# Revit family: Gleitschlitte Typ A, höhe h=100mm, Ø219 bis Ø457mm, o.D.
name_source: partatom
category: HLS-Bauteile
revit_build: Autodesk Revit 2018 (Build: 20190510_1515(x64)
units: mm (PartAtom-declared; Revit-internal decimal feet)

## family parameters
Arbeitsebenenbasiert = Ja
Beim Laden mit Abzugskörper schneiden = Nein
Bemaßung runder Anschluss = Durchmesser verwenden
Gemeinsam genutzt = Ja
Immer vertikal = Nein
Klassifizierung = Keine
Raumberechnungspunkt = Nein
Teiletyp = Normal

## types (11) — shared parameters
Breite Schellenband = 50 mm
Fabrikat = MEFA
Kurztext1 = Gleitschlitten A 50 x 5 mm
L = 190 mm
Länge Unterbau = 270 mm
Mengeneinheit = St
Schalldämmeinlage = ohne Dämmung
Sicherheitsfaktor = 1.54
Stärke Schellenband = 5 mm
Verschluss = Schraube + Mutter
Verschluss-Schraube = M12
Vorgabe-Ansicht = 1219 mm
vpe = 1
zero-valued in all types: Dämmstärke

## per-type parameters (varying)
| type | A (Breite) | Achshöhe | Artikelnummer | Breite Unterbau | EAN | Flachmaterial | Gewicht | Gewicht pro Bauteil | Kurztext2 | RS Titan Ø219 bis 508 | Rohraußendurchmesser | Schuh | Stärke Material |
| Gleitschlitten TypA, h=100mm, o.D., Ø219mm | 114 mm  [stored 0.374016 ft] | 210 mm | 110afa0219 | 230 mm | 4250928461575 | Flachmaterial nach DIN (50-5 und 70-8) : für Ø219 | 8.68 kg | 8.68 kg | 219 mm o. Dämm. fsv | Rohrschelle Titan HD, ohne AG, o.D, Ø219 bis Ø508 30Grad ok : Titan HD, Ø219, 30Grad | 219 mm  [stored 0.718504 ft] | TL-Fuß für Gleitschl.2Lo.14 : 9000816 | 6 mm  [stored 0.019685 ft] |
| Gleitschlitten TypA, h=100mm, o.D., Ø225mm | 114 mm  [stored 0.374016 ft] | 213 mm | 110afa0225 | 230 mm | 4250928461582 | Flachmaterial nach DIN (50-5 und 70-8) : für Ø225 | 8.77 kg | 8.77 kg | 228 mm o. Dämm. fsv | Rohrschelle Titan HD, ohne AG, o.D, Ø219 bis Ø508 30Grad ok : Titan HD, Ø225, 30Grad | 228 mm  [stored 0.748031 ft] | TL-Fuß für Gleitschl.2Lo.14 : 9000816 | 6 mm  [stored 0.019685 ft] |
| Gleitschlitten TypA, h=100mm, o.D., Ø273mm | 128 mm  [stored 0.419948 ft] | 237 mm | 110afa0273 | 244 mm | 4250928461599 | Flachmaterial nach DIN (50-5 und 70-8) : für Ø273 | 9.50 kg | 9.50 kg | 273 mm o. Dämm. fsv | Rohrschelle Titan HD, ohne AG, o.D, Ø219 bis Ø508 30Grad ok : Titan HD, Ø273, 30Grad | 273 mm  [stored 0.895669 ft] | TL-Fuß für Gleitschl.2Lo.14 : 9000816 | 6 mm  [stored 0.019685 ft] |
| Gleitschlitten TypA, h=100mm, o.D., Ø280mm | 128 mm  [stored 0.419948 ft] | 240 mm | 110afa0280 | 244 mm | 4250928461605 | Flachmaterial nach DIN (50-5 und 70-8) : für Ø280 | 9.60 kg | 9.60 kg | 280 mm o. Dämm. fsv | Rohrschelle Titan HD, ohne AG, o.D, Ø219 bis Ø508 30Grad ok : Titan HD, Ø280, 30Grad | 280 mm  [stored 0.918635 ft] | TL-Fuß für Gleitschl.2Lo.14 : 9000816 | 6 mm  [stored 0.019685 ft] |
| Gleitschlitten TypA, h=100mm, o.D., Ø315mm | 138 mm  [stored 0.452756 ft] | 258 mm | 110afa0315 | 254 mm | 4250928461612 | Flachmaterial nach DIN (50-5 und 70-8) : für Ø315 | 10.13 kg | 10.13 kg | 315 mm o. Dämm. fsv | Rohrschelle Titan HD, ohne AG, o.D, Ø219 bis Ø508 30Grad ok : Titan HD, Ø315, 30Grad | 315 mm  [stored 1.03346 ft] | TL-Fuß für Gleitschl.2Lo.14 : 9000816 | 6 mm  [stored 0.019685 ft] |
| Gleitschlitten TypA, h=100mm, o.D., Ø324mm | 138 mm  [stored 0.452756 ft] | 262 mm | 110afa0324 | 254 mm | 4250928461629 | Flachmaterial nach DIN (50-5 und 70-8) : für Ø324 | 10.26 kg | 10.26 kg | 324 mm o. Dämm. fsv | Rohrschelle Titan HD, ohne AG, o.D, Ø219 bis Ø508 30Grad ok : Titan HD, Ø324, 30Grad | 324 mm  [stored 1.06299 ft] | TL-Fuß für Gleitschl.2Lo.14 : 9000816 | 6 mm  [stored 0.019685 ft] |
| Gleitschlitten TypA, h=100mm, o.D., Ø356mm | 146 mm  [stored 0.479003 ft] | 278 mm | 110afa0356 | 262 mm | 4250928461636 | Flachmaterial nach DIN (50-5 und 70-8) : für Ø356 | 10.73 kg | 10.73 kg | 356 mm o. Dämm. fsv | Rohrschelle Titan HD, ohne AG, o.D, Ø219 bis Ø508 30Grad ok : Titan HD, Ø356, 30Grad | 356 mm  [stored 1.16798 ft] | TL-Fuß für Gleitschl.2Lo.14 : 9000816 | 6 mm  [stored 0.019685 ft] |
| Gleitschlitten TypA, h=100mm, o.D., Ø400mm | 177 mm  [stored 0.580709 ft] | 300 mm | 110afa0400 | 293 mm | 4250928461643 | Flachmaterial nach DIN (50-5 und 70-8) : für Ø400 | 13.85 kg | 13.85 kg | 400 mm o. Dämm. fsv | Rohrschelle Titan HD, ohne AG, o.D, Ø219 bis Ø508 30Grad ok : Titan HD, Ø400, 30Grad | 400 mm  [stored 1.31234 ft] | TL-Fuß für Gleitschl.2Lo.14 : 9000817 | 8 mm  [stored 0.0262467 ft] |
| Gleitschlitten TypA, h=100mm, o.D., Ø406mm | 177 mm  [stored 0.580709 ft] | 303 mm | 110afa0406 | 293 mm | 4250928461650 | Flachmaterial nach DIN (50-5 und 70-8) : für Ø406.4 | 13.93 kg | 13.93 kg | 406 mm o. Dämm. fsv | Rohrschelle Titan HD, ohne AG, o.D, Ø219 bis Ø508 30Grad ok : Titan HD, Ø406, 30Grad | 406 mm  [stored 1.33202 ft] | TL-Fuß für Gleitschl.2Lo.14 : 9000817 | 8 mm  [stored 0.0262467 ft] |
| Gleitschlitten TypA, h=100mm, o.D., Ø450mm | 189 mm  [stored 0.620079 ft] | 325 mm | 110afa0450 | 305 mm | 4250928461667 | Flachmaterial nach DIN (50-5 und 70-8) : für Ø450 | 14.66 kg | 14.66 kg | 450 mm o. Dämm. fsv | Rohrschelle Titan HD, ohne AG, o.D, Ø219 bis Ø508 30Grad ok : Titan HD, Ø450, 30Grad | 450 mm  [stored 1.47638 ft] | TL-Fuß für Gleitschl.2Lo.14 : 9000817 | 8 mm  [stored 0.0262467 ft] |
| Gleitschlitten TypA, h=100mm, o.D., Ø457mm | 189 mm  [stored 0.620079 ft] | 329 mm | 110afa0457 | 305 mm | 4250928461674 | Flachmaterial nach DIN (50-5 und 70-8) : für Ø457 | 14.76 kg | 14.76 kg | 457 mm o. Dämm. fsv | Rohrschelle Titan HD, ohne AG, o.D, Ø219 bis Ø508 30Grad ok : Titan HD, Ø457, 30Grad | 457 mm  [stored 1.49934 ft] | TL-Fuß für Gleitschl.2Lo.14 : 9000817 | 8 mm  [stored 0.0262467 ft] |

note: [stored X ft] marks values corroborated as IEEE doubles in the binary element streams (Revit-internal decimal feet)

## geometry (parser evidence)
native form markers: Sweep x7
no freeform markers — native parametric forms only
